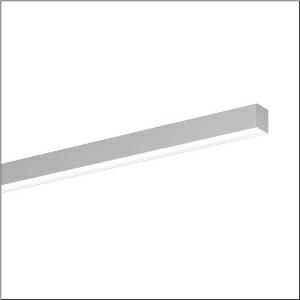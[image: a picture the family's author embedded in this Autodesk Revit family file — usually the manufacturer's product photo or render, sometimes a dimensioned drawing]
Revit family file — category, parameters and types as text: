
# Revit family: silica_21_51mx20dc35sb
name_source: partatom
category: Lighting Fixtures
units: mm (PartAtom-declared; Revit-internal decimal feet)

## family parameters
Cut with Voids When Loaded = No
Host = Face
Light Source = No
Part Type = Normal
Room Calculation Point = No
Round Connector Dimension = Use Diameter
Shared = No

## types (1)
- --- (1 x LED, 6000 lm, 42.6 W, 3000K)
    Apparent Load = 43 VA
    CIE Flux Codes = 48 79 96 100 100
    Color Rendering = 80
    Color Temperature = 3000K
    Default Elevation = 1800 mm
    Description = Silica 21, office luminaire, primary optical cover: cover, of PMMA, opal, light emission: direct distribution, primary light characteristic: symmetric, installation type: surface-mounted, LED, rated luminous flux: 6.000lm, luminous efficacy: 141lm/W, light colour: 830, colour temperature: 3000K, control gear: DALI 2, with terminal, 3+2-pole, max. 2.5mm², mains connection: 220..240V, AC, 50/60Hz, rated input power: 42.6W, luminaire housing, of aluminium, metallic grey (RAL 9006), length: 3.004mm, width: 53mm, height: 53mm, protection rating (complete): IP20, insulation class (complete): insulation class I (protective earthing), certification: CE, permissible operating ambient temperature: 0..+35°C, standard: EN 50419, packaging unit: 1 piece
    Height = 53 mm
    Lamp = 1 x LED
    Lamp Light Flux = 6000 lm
    Lamp Power = 42.6 W
    Lamp count = 1
    Length = 3004 mm
    Luminous efficacy = 141 lm/W
    Manufacturer = Siteco
    ModVariant = No
    Model = 51MX20DC35SB
    Mounting Place = Ceiling
    Mounting Type = Surface mounted
    Number of Poles = 1
    OnlyDefault = Yes
    Power Factor = 1
    Product Name = Silica 21
    Product group = office luminaire | ceiling mounted
    ProductGroupID = 301
    Protection Class = Protection class I
    Protection Degree = IP 20
    RLX_Detail_Level = 1
    RLX_Emergency_Light_Flux = 0 lm
    RLX_Emergency_Type = 0
    RLX_Emergency_Type_DB = No
    RlxData = <blob elided: 26337 chars, md5=e31dc48f>
    Socket = socket
    Standby Power = 0 W
    System Light Flux = 6000 lm
    System Power = 43 W
    Type Comments = factory setting: luminous flux: 100 % | dim-lin: 254 | 233 mA
    Type Image = l_1335933.jpg
    URL = http://relux.com
    VarID = @adj_117885
    Voltage = 0 V
    Weight = 0.00 kg
    Width = 53 mm

## geometry (parser evidence)
native form markers: Blend x4, Sweep x10
no freeform markers — native parametric forms only
